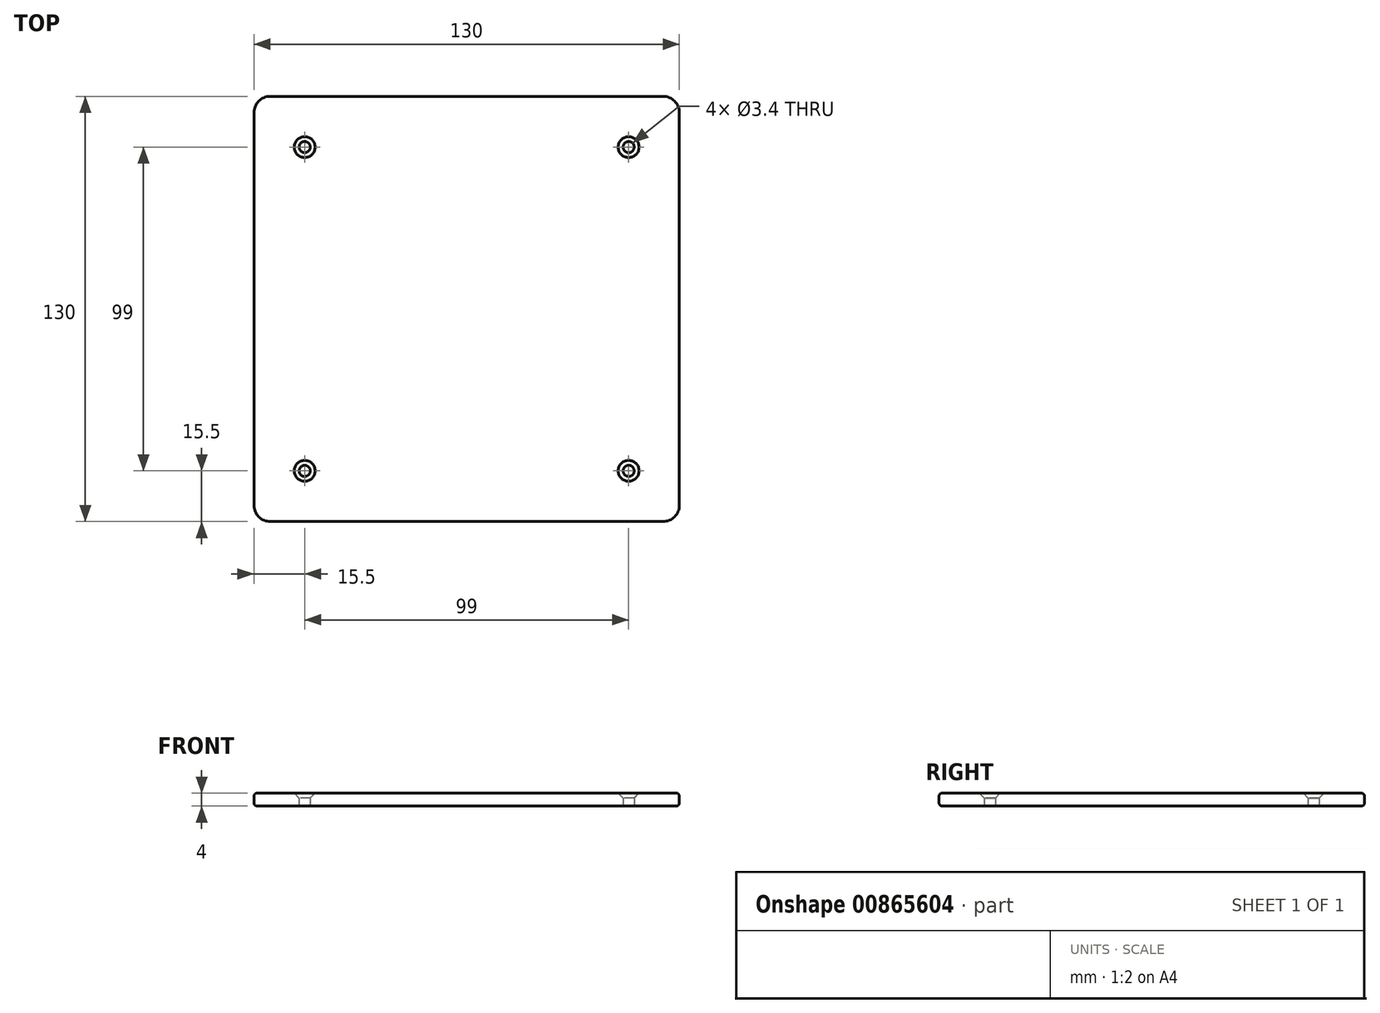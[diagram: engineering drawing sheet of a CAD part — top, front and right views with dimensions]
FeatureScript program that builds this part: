
annotation { "Feature Type Name" : "Feature", "Feature Type Description" : "" }
export const myFeature = defineFeature(function(context is Context, id is Id, definition is map)
    precondition{}
    {
        {
            var Q0;
            Q0=qCreatedBy(makeId("Top.planeOp"),FACE);
            var sketch = newSketch(context, id + "F0", { "sketchPlane" : qUnion([Q0])});
            skLineSegment(sketch, "E0.bottom", {"start": v(-65, 65) * mm, "end": v(65, 65) * mm});
            skLineSegment(sketch, "E0.top", {"start": v(-65, -65) * mm, "end": v(65, -65) * mm});
            skLineSegment(sketch, "E0.left", {"start": v(-65, 65) * mm, "end": v(-65, -65) * mm});
            skLineSegment(sketch, "E0.right", {"start": v(65, 65) * mm, "end": v(65, -65) * mm});
            skCircle(sketch, "E1", {"center": v(-49.5, 49.5) * mm, "radius": 1.7 * mm});
            skCircle(sketch, "E2.MirrorC", {"center": v(49.5, 49.5) * mm, "radius": 1.7 * mm});
            skCircle(sketch, "E3.MirrorC", {"center": v(-49.5, -49.5) * mm, "radius": 1.7 * mm});
            skCircle(sketch, "E4.MirrorC", {"center": v(49.5, -49.5) * mm, "radius": 1.7 * mm});
            skSolve(sketch);
        }
        {
            var Q0;
            Q0=makeQuery(id+"F0.imprint","IMPRINT",FACE,{"disambiguationData":[TD([[makeQuery(id+"F0.imprint","IMPRINT",EDGE,{"derivedFrom":sQuery(id+"F0.wireOp",EDGE,"E0.bottom")}),-1.0]])]});
            extrude(context, id + "F1", {"entities" : qUnion([Q0]), "depth" : 4 * mm, "offsetDistance" : 25 * mm});
        }
        {
            var Q0;
            Q0=makeQuery(id+"F1.opExtrude","SWEPT_EDGE",EDGE,{"disambiguationData":[OSD([sQuery(id+"F0.wireOp",EDGE,"E0.bottom"),sQuery(id+"F0.wireOp",EDGE,"E0.right")])]});
            var Q1;
            Q1=makeQuery(id+"F1.opExtrude","SWEPT_EDGE",EDGE,{"disambiguationData":[OSD([sQuery(id+"F0.wireOp",EDGE,"E0.top"),sQuery(id+"F0.wireOp",EDGE,"E0.right")])]});
            var Q2;
            Q2=makeQuery(id+"F1.opExtrude","SWEPT_EDGE",EDGE,{"disambiguationData":[OSD([sQuery(id+"F0.wireOp",EDGE,"E0.top"),sQuery(id+"F0.wireOp",EDGE,"E0.left")])]});
            var Q3;
            Q3=makeQuery(id+"F1.opExtrude","SWEPT_EDGE",EDGE,{"disambiguationData":[OSD([sQuery(id+"F0.wireOp",EDGE,"E0.bottom"),sQuery(id+"F0.wireOp",EDGE,"E0.left")])]});
            fillet(context, id + "F2", {"entities" : qUnion([Q0, Q1, Q2, Q3]), "radius" : 5 * mm, "tangentPropagation" : true, "allowEdgeOverflow" : false});
        }
        {
            var Q0;
            Q0=makeQuery(id+"F1.opExtrude","CAP_EDGE",EDGE,{"disambiguationData":[OSD([sQuery(id+"F0.wireOp",EDGE,"E0.right")])],"isStart":false});
            var Q1;
            Q1=makeQuery(id+"F1.opExtrude","CAP_EDGE",EDGE,{"disambiguationData":[OSD([sQuery(id+"F0.wireOp",EDGE,"E0.right")])],"isStart":true});
            fillet(context, id + "F3", {"entities" : qUnion([Q0, Q1]), "radius" : 1 * mm, "tangentPropagation" : true, "allowEdgeOverflow" : false});
        }
        {
            var Q0;
            Q0=makeQuery(id+"F1.opExtrude","CAP_EDGE",EDGE,{"disambiguationData":[OSD([sQuery(id+"F0.wireOp",EDGE,"E1")])],"isStart":false});
            var Q1;
            Q1=makeQuery(id+"F1.opExtrude","CAP_EDGE",EDGE,{"disambiguationData":[OSD([sQuery(id+"F0.wireOp",EDGE,"E2.MirrorC")])],"isStart":false});
            var Q2;
            Q2=makeQuery(id+"F1.opExtrude","CAP_EDGE",EDGE,{"disambiguationData":[OSD([sQuery(id+"F0.wireOp",EDGE,"E4.MirrorC")])],"isStart":false});
            var Q3;
            Q3=makeQuery(id+"F1.opExtrude","CAP_EDGE",EDGE,{"disambiguationData":[OSD([sQuery(id+"F0.wireOp",EDGE,"E3.MirrorC")])],"isStart":false});
            chamfer(context, id + "F4", {"entities" : qUnion([Q0, Q1, Q2, Q3]), "width" : 1.5 * mm, "tangentPropagation" : true});
        }
    });
